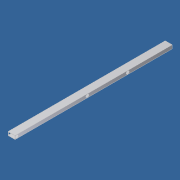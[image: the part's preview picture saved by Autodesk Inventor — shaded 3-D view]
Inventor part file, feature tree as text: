
AUTODESK INVENTOR PART (.ipt)
format: ipt  version: 2012 (Build 160160000, 160)  size: 94,720 bytes
history: native  units: in
note: dims shown in document units (in); Inventor stores cm internally (conversion verified against a paired STEP export)
features: hole x2, extrude x1, pattern_linear x1, sketch x1
ambient origin geometry x8: Origin, YZ Plane, XZ Plane, XY Plane, X Axis, Y Axis, Z Axis, Center Point
bodies: Solid1 (feature_tree)
feature tree (5):
  extrude  "Extrusion1"  Depth=3.5in
  hole  "Hole1"  [1 undecoded]
  pattern_linear  "Rectangular Pattern1"  Spacing1=78.0in  [1 undecoded]
  hole  "Hole2"  [1 undecoded]
  sketch  "Sketch1"  dims[d0=0.125in d1=3.5in d2=1.75in d3=78.0in d4=0.0in d5=0.875in d6=0.875in d7=1.5in d8=0.75in d9=0.375in d10=0.25in d11=0.5635in d12=1.0in d13=0.8108in d14=0.7874in d16=35.0in d17=22.125in d18=0.875in d19=1.5in d20=0.75in d21=0.375in d22=0.25in d23=0.5635in d24=1.0in d25=0.8108in]
note: 3 required parameter values undecoded (feature->parameter linkage not recoverable at this tier; creation-order binding heuristic only, values carry confidence <= 0.55)
